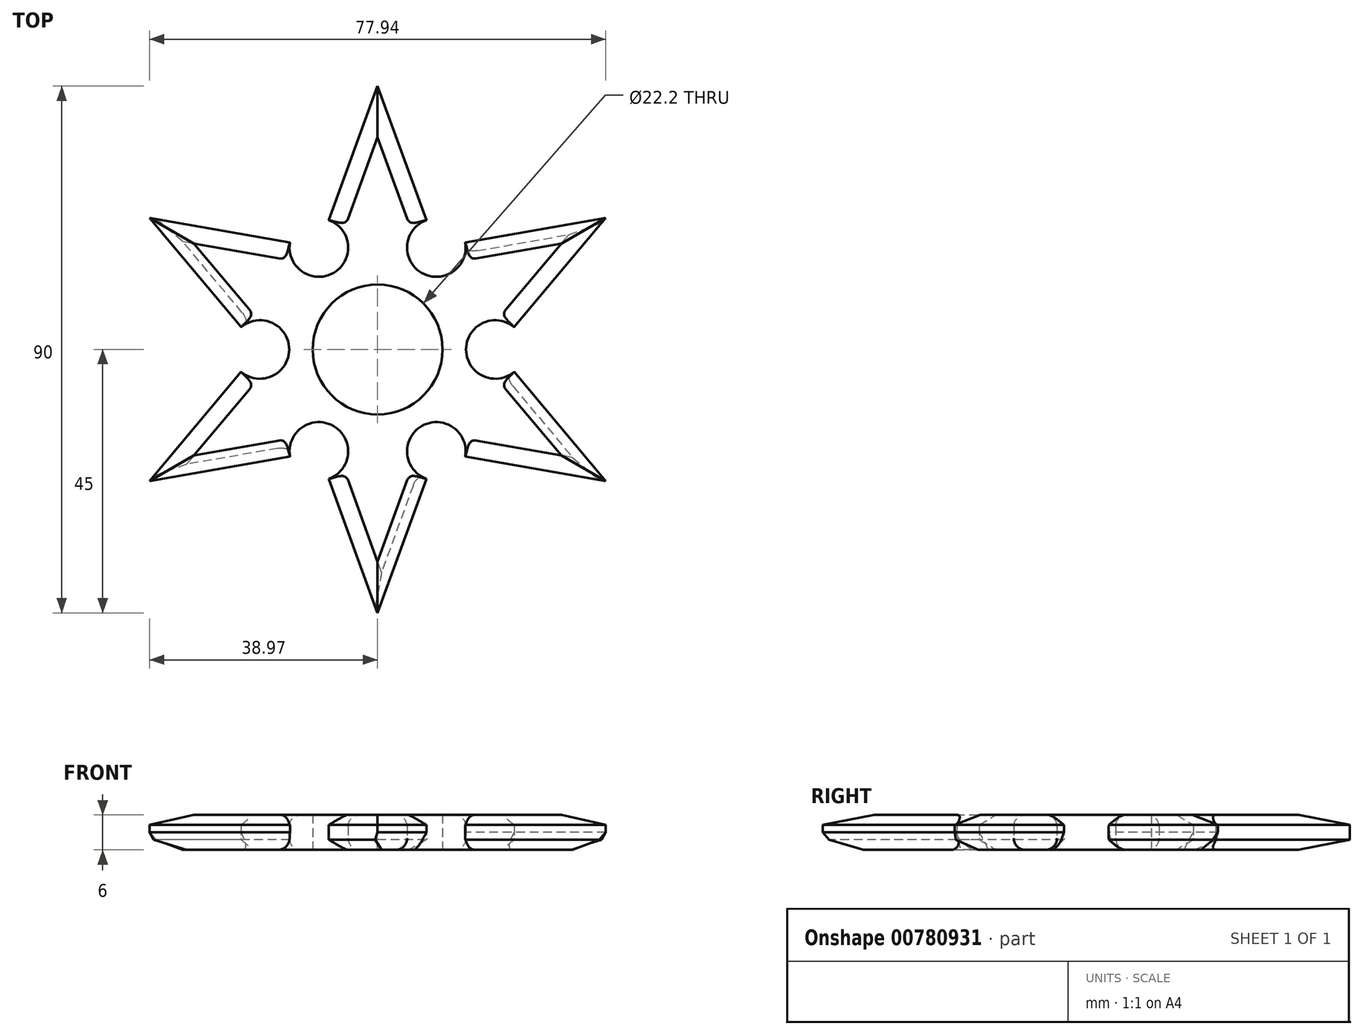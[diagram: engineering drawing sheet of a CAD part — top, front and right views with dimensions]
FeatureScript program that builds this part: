
annotation { "Feature Type Name" : "Feature", "Feature Type Description" : "" }
export const myFeature = defineFeature(function(context is Context, id is Id, definition is map)
    precondition{}
    {
        {
            var Q0;
            Q0=qCreatedBy(makeId("Top.planeOp"),FACE);
            var sketch = newSketch(context, id + "F0", { "sketchPlane" : qUnion([Q0])});
            skCircle(sketch, "E0", {"center": v(0, 0) * mm, "radius": 11.1 * mm});
            skLineSegment(sketch, "E1", {"start": v(0, 45) * mm, "end": v(-8.34, 22.1) * mm});
            skLineSegment(sketch, "E2.MirrorCS", {"start": v(0, 45) * mm, "end": v(8.34, 22.1) * mm});
            skLineSegment(sketch, "E3.1.0", {"start": v(-38.97, 22.5) * mm, "end": v(-14.97, 18.27) * mm});
            skLineSegment(sketch, "E3.1.1", {"start": v(-38.97, 22.5) * mm, "end": v(-23.31, 3.83) * mm});
            skLineSegment(sketch, "E3.2.0", {"start": v(-38.97, -22.5) * mm, "end": v(-23.31, -3.83) * mm});
            skLineSegment(sketch, "E3.2.1", {"start": v(-38.97, -22.5) * mm, "end": v(-14.97, -18.27) * mm});
            skLineSegment(sketch, "E3.3.0", {"start": v(0, -45) * mm, "end": v(-8.34, -22.1) * mm});
            skLineSegment(sketch, "E3.3.1", {"start": v(0, -45) * mm, "end": v(8.34, -22.1) * mm});
            skLineSegment(sketch, "E3.4.0", {"start": v(38.97, -22.5) * mm, "end": v(14.97, -18.27) * mm});
            skLineSegment(sketch, "E3.4.1", {"start": v(38.97, -22.5) * mm, "end": v(23.31, -3.83) * mm});
            skLineSegment(sketch, "E3.5.0", {"start": v(38.97, 22.5) * mm, "end": v(23.31, 3.83) * mm});
            skLineSegment(sketch, "E3.5.1", {"start": v(38.97, 22.5) * mm, "end": v(14.97, 18.27) * mm});
            skArc(sketch, "E4", {"start": v(-14.97, 18.27) * mm, "mid": v(-7.55, 13.08) * mm, "end": v(-8.34, 22.1) * mm});
            skArc(sketch, "E5.1.0", {"start": v(-23.31, -3.83) * mm, "mid": v(-15.1, 0) * mm, "end": v(-23.31, 3.83) * mm});
            skArc(sketch, "E5.2.0", {"start": v(-8.34, -22.1) * mm, "mid": v(-7.55, -13.08) * mm, "end": v(-14.97, -18.27) * mm});
            skArc(sketch, "E5.3.0", {"start": v(14.97, -18.27) * mm, "mid": v(7.55, -13.08) * mm, "end": v(8.34, -22.1) * mm});
            skArc(sketch, "E5.4.0", {"start": v(23.31, 3.83) * mm, "mid": v(15.1, 0) * mm, "end": v(23.31, -3.83) * mm});
            skArc(sketch, "E5.5.0", {"start": v(8.34, 22.1) * mm, "mid": v(7.55, 13.08) * mm, "end": v(14.97, 18.27) * mm});
            skSolve(sketch);
        }
        {
            var Q0;
            Q0=makeQuery(id+"F0.imprint","IMPRINT",FACE,{"disambiguationData":[TD([[makeQuery(id+"F0.imprint","IMPRINT",EDGE,{"derivedFrom":sQuery(id+"F0.wireOp",EDGE,"E0")}),-1.0]])]});
            extrude(context, id + "F1", {"entities" : qUnion([Q0]), "depth" : 6 * mm, "offsetDistance" : 25 * mm});
        }
        {
            var Q0;
            Q0=makeQuery(id+"F1.opExtrude","CAP_EDGE",EDGE,{"disambiguationData":[OSD([sQuery(id+"F0.wireOp",EDGE,"E1")])],"isStart":false});
            var Q1;
            Q1=makeQuery(id+"F1.opExtrude","CAP_EDGE",EDGE,{"disambiguationData":[OSD([sQuery(id+"F0.wireOp",EDGE,"E2.MirrorCS")])],"isStart":false});
            var Q2;
            Q2=makeQuery(id+"F1.opExtrude","CAP_EDGE",EDGE,{"disambiguationData":[OSD([sQuery(id+"F0.wireOp",EDGE,"E3.5.1")])],"isStart":false});
            var Q3;
            Q3=makeQuery(id+"F1.opExtrude","CAP_EDGE",EDGE,{"disambiguationData":[OSD([sQuery(id+"F0.wireOp",EDGE,"E3.5.0")])],"isStart":false});
            var Q4;
            Q4=makeQuery(id+"F1.opExtrude","CAP_EDGE",EDGE,{"disambiguationData":[OSD([sQuery(id+"F0.wireOp",EDGE,"E3.4.1")])],"isStart":false});
            var Q5;
            Q5=makeQuery(id+"F1.opExtrude","CAP_EDGE",EDGE,{"disambiguationData":[OSD([sQuery(id+"F0.wireOp",EDGE,"E3.4.0")])],"isStart":false});
            var Q6;
            Q6=makeQuery(id+"F1.opExtrude","CAP_EDGE",EDGE,{"disambiguationData":[OSD([sQuery(id+"F0.wireOp",EDGE,"E3.3.1")])],"isStart":false});
            var Q7;
            Q7=makeQuery(id+"F1.opExtrude","CAP_EDGE",EDGE,{"disambiguationData":[OSD([sQuery(id+"F0.wireOp",EDGE,"E3.3.0")])],"isStart":false});
            var Q8;
            Q8=makeQuery(id+"F1.opExtrude","CAP_EDGE",EDGE,{"disambiguationData":[OSD([sQuery(id+"F0.wireOp",EDGE,"E3.2.1")])],"isStart":false});
            var Q9;
            Q9=makeQuery(id+"F1.opExtrude","CAP_EDGE",EDGE,{"disambiguationData":[OSD([sQuery(id+"F0.wireOp",EDGE,"E3.2.0")])],"isStart":false});
            var Q10;
            Q10=makeQuery(id+"F1.opExtrude","CAP_EDGE",EDGE,{"disambiguationData":[OSD([sQuery(id+"F0.wireOp",EDGE,"E3.1.1")])],"isStart":false});
            var Q11;
            Q11=makeQuery(id+"F1.opExtrude","CAP_EDGE",EDGE,{"disambiguationData":[OSD([sQuery(id+"F0.wireOp",EDGE,"E3.1.0")])],"isStart":false});
            var Q12;
            Q12=makeQuery(id+"F1.opExtrude","CAP_EDGE",EDGE,{"disambiguationData":[OSD([sQuery(id+"F0.wireOp",EDGE,"E3.3.1")])],"isStart":true});
            var Q13;
            Q13=makeQuery(id+"F1.opExtrude","CAP_EDGE",EDGE,{"disambiguationData":[OSD([sQuery(id+"F0.wireOp",EDGE,"E3.3.0")])],"isStart":true});
            var Q14;
            Q14=makeQuery(id+"F1.opExtrude","CAP_EDGE",EDGE,{"disambiguationData":[OSD([sQuery(id+"F0.wireOp",EDGE,"E3.2.1")])],"isStart":true});
            var Q15;
            Q15=makeQuery(id+"F1.opExtrude","CAP_EDGE",EDGE,{"disambiguationData":[OSD([sQuery(id+"F0.wireOp",EDGE,"E3.2.0")])],"isStart":true});
            var Q16;
            Q16=makeQuery(id+"F1.opExtrude","CAP_EDGE",EDGE,{"disambiguationData":[OSD([sQuery(id+"F0.wireOp",EDGE,"E3.1.1")])],"isStart":true});
            var Q17;
            Q17=makeQuery(id+"F1.opExtrude","CAP_EDGE",EDGE,{"disambiguationData":[OSD([sQuery(id+"F0.wireOp",EDGE,"E3.1.0")])],"isStart":true});
            var Q18;
            Q18=makeQuery(id+"F1.opExtrude","CAP_EDGE",EDGE,{"disambiguationData":[OSD([sQuery(id+"F0.wireOp",EDGE,"E1")])],"isStart":true});
            var Q19;
            Q19=makeQuery(id+"F1.opExtrude","CAP_EDGE",EDGE,{"disambiguationData":[OSD([sQuery(id+"F0.wireOp",EDGE,"E2.MirrorCS")])],"isStart":true});
            var Q20;
            Q20=makeQuery(id+"F1.opExtrude","CAP_EDGE",EDGE,{"disambiguationData":[OSD([sQuery(id+"F0.wireOp",EDGE,"E3.5.1")])],"isStart":true});
            var Q21;
            Q21=makeQuery(id+"F1.opExtrude","CAP_EDGE",EDGE,{"disambiguationData":[OSD([sQuery(id+"F0.wireOp",EDGE,"E3.5.0")])],"isStart":true});
            var Q22;
            Q22=makeQuery(id+"F1.opExtrude","CAP_EDGE",EDGE,{"disambiguationData":[OSD([sQuery(id+"F0.wireOp",EDGE,"E3.4.1")])],"isStart":true});
            var Q23;
            Q23=makeQuery(id+"F1.opExtrude","CAP_EDGE",EDGE,{"disambiguationData":[OSD([sQuery(id+"F0.wireOp",EDGE,"E3.4.0")])],"isStart":true});
            chamfer(context, id + "F2", {"entities" : qUnion([Q0, Q1, Q2, Q3, Q4, Q5, Q6, Q7, Q8, Q9, Q10, Q11, Q12, Q13, Q14, Q15, Q16, Q17, Q18, Q19, Q20, Q21, Q22, Q23]), "chamferType" : ChamferType.OFFSET_ANGLE, "width" : 3 * mm, "oppositeDirection" : false, "angle" : 30 * degree, "tangentPropagation" : true});
        }
        {
            var Q0;
            Q0=makeQuery(id+"F1.opExtrude","CAP_EDGE",EDGE,{"disambiguationData":[OSD([sQuery(id+"F0.wireOp",EDGE,"E5.3.0")])],"isStart":false});
            var Q1;
            Q1=makeQuery(id+"F1.opExtrude","CAP_EDGE",EDGE,{"disambiguationData":[OSD([sQuery(id+"F0.wireOp",EDGE,"E5.4.0")])],"isStart":false});
            var Q2;
            Q2=makeQuery(id+"F1.opExtrude","CAP_EDGE",EDGE,{"disambiguationData":[OSD([sQuery(id+"F0.wireOp",EDGE,"E5.2.0")])],"isStart":false});
            var Q3;
            Q3=makeQuery(id+"F1.opExtrude","CAP_EDGE",EDGE,{"disambiguationData":[OSD([sQuery(id+"F0.wireOp",EDGE,"E5.1.0")])],"isStart":false});
            var Q4;
            Q4=makeQuery(id+"F1.opExtrude","CAP_EDGE",EDGE,{"disambiguationData":[OSD([sQuery(id+"F0.wireOp",EDGE,"E4")])],"isStart":false});
            var Q5;
            Q5=makeQuery(id+"F1.opExtrude","CAP_EDGE",EDGE,{"disambiguationData":[OSD([sQuery(id+"F0.wireOp",EDGE,"E5.5.0")])],"isStart":false});
            var Q6;
            Q6=makeQuery(id+"F1.opExtrude","CAP_EDGE",EDGE,{"disambiguationData":[OSD([sQuery(id+"F0.wireOp",EDGE,"E5.2.0")])],"isStart":true});
            var Q7;
            Q7=makeQuery(id+"F1.opExtrude","CAP_EDGE",EDGE,{"disambiguationData":[OSD([sQuery(id+"F0.wireOp",EDGE,"E5.3.0")])],"isStart":true});
            var Q8;
            Q8=makeQuery(id+"F1.opExtrude","CAP_EDGE",EDGE,{"disambiguationData":[OSD([sQuery(id+"F0.wireOp",EDGE,"E5.4.0")])],"isStart":true});
            var Q9;
            Q9=makeQuery(id+"F1.opExtrude","CAP_EDGE",EDGE,{"disambiguationData":[OSD([sQuery(id+"F0.wireOp",EDGE,"E5.5.0")])],"isStart":true});
            var Q10;
            Q10=makeQuery(id+"F1.opExtrude","CAP_EDGE",EDGE,{"disambiguationData":[OSD([sQuery(id+"F0.wireOp",EDGE,"E4")])],"isStart":true});
            var Q11;
            Q11=makeQuery(id+"F1.opExtrude","CAP_EDGE",EDGE,{"disambiguationData":[OSD([sQuery(id+"F0.wireOp",EDGE,"E5.1.0")])],"isStart":true});
            fillet(context, id + "F3", {"entities" : qUnion([Q0, Q1, Q2, Q3, Q4, Q5, Q6, Q7, Q8, Q9, Q10, Q11]), "radius" : 2 * mm, "tangentPropagation" : true, "allowEdgeOverflow" : false});
        }
    });
